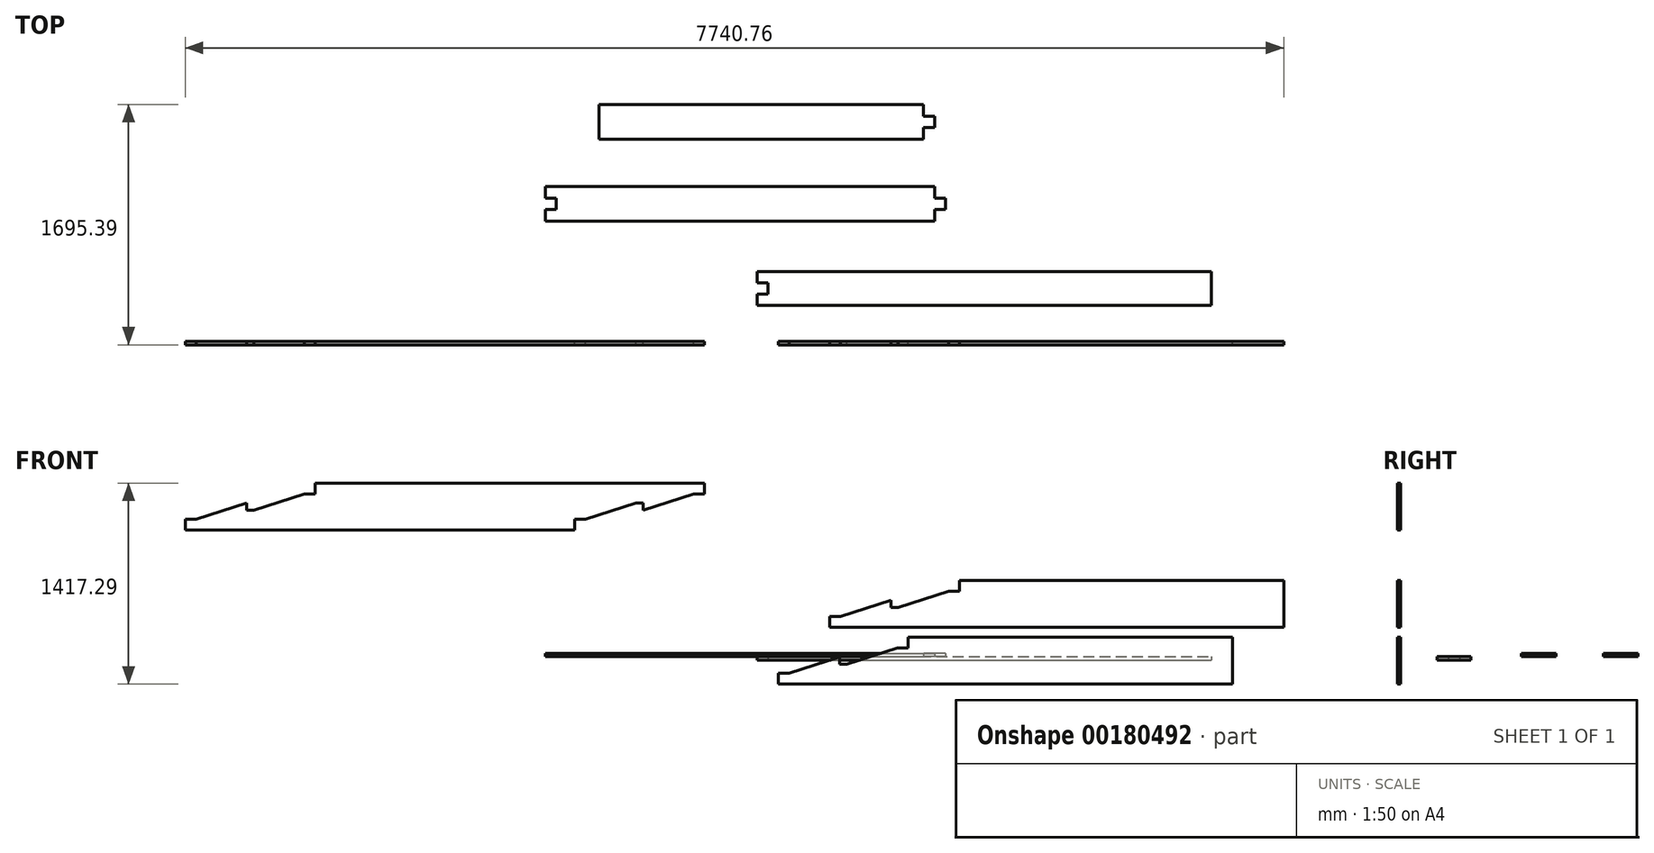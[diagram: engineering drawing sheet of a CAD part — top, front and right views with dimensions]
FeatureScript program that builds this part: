
annotation { "Feature Type Name" : "Feature", "Feature Type Description" : "" }
export const myFeature = defineFeature(function(context is Context, id is Id, definition is map)
    precondition{}
    {
        {
            var Q0;
            Q0=qCreatedBy(makeId("Front.planeOp"),FACE);
            var sketch = newSketch(context, id + "F0", { "sketchPlane" : qUnion([Q0])});
            skLineSegment(sketch, "E0.bottom", {"start": v(-614.36, 159.8) * mm, "end": v(1671.64, 159.8) * mm});
            skLineSegment(sketch, "E0.top", {"start": v(-1528.76, -170.4) * mm, "end": v(1671.64, -170.4) * mm});
            skLineSegment(sketch, "E0.left", {"start": v(-1528.76, -94.2) * mm, "end": v(-1528.76, -170.4) * mm});
            skLineSegment(sketch, "E0.right", {"start": v(1671.64, 159.8) * mm, "end": v(1671.64, -170.4) * mm});
            skLineSegment(sketch, "E1", {"start": v(-1528.76, -94.2) * mm, "end": v(-1452.56, -94.2) * mm});
            skLineSegment(sketch, "E2", {"start": v(-1452.56, -94.2) * mm, "end": v(-1096.96, 20.1) * mm});
            skLineSegment(sketch, "E3", {"start": v(-1096.96, 20.1) * mm, "end": v(-1096.96, -30.7) * mm});
            skLineSegment(sketch, "E4", {"start": v(-1096.96, -30.7) * mm, "end": v(-1046.16, -30.7) * mm});
            skLineSegment(sketch, "E5", {"start": v(-1046.16, -30.7) * mm, "end": v(-690.56, 83.6) * mm});
            skLineSegment(sketch, "E6", {"start": v(-690.56, 83.6) * mm, "end": v(-614.36, 83.6) * mm});
            skLineSegment(sketch, "E7", {"start": v(-614.36, 83.6) * mm, "end": v(-614.36, 159.8) * mm});
            skPoint(sketch, "E8.orphan", {"position": v(-1528.76, 159.8) * mm});
            skLineSegment(sketch, "E9.bottom", {"start": v(-254.29, 561.34) * mm, "end": v(2031.71, 561.34) * mm});
            skLineSegment(sketch, "E9.top", {"start": v(-1168.69, 231.14) * mm, "end": v(2031.71, 231.14) * mm});
            skLineSegment(sketch, "E9.left", {"start": v(-1168.69, 307.34) * mm, "end": v(-1168.69, 231.14) * mm});
            skLineSegment(sketch, "E9.right", {"start": v(2031.71, 561.34) * mm, "end": v(2031.71, 231.14) * mm});
            skLineSegment(sketch, "E10", {"start": v(-1168.69, 307.34) * mm, "end": v(-1092.49, 307.34) * mm});
            skLineSegment(sketch, "E11", {"start": v(-1092.49, 307.34) * mm, "end": v(-736.89, 421.64) * mm});
            skLineSegment(sketch, "E12", {"start": v(-736.89, 421.64) * mm, "end": v(-736.89, 370.84) * mm});
            skLineSegment(sketch, "E13", {"start": v(-736.89, 370.84) * mm, "end": v(-686.09, 370.84) * mm});
            skLineSegment(sketch, "E14", {"start": v(-686.09, 370.84) * mm, "end": v(-330.49, 485.14) * mm});
            skLineSegment(sketch, "E15", {"start": v(-330.49, 485.14) * mm, "end": v(-254.29, 485.14) * mm});
            skLineSegment(sketch, "E16", {"start": v(-254.29, 485.14) * mm, "end": v(-254.29, 561.34) * mm});
            skPoint(sketch, "E17.orphan", {"position": v(-1168.69, 561.34) * mm});
            skSolve(sketch);
        }
        {
            var Q0;
            Q0=makeQuery(id+"F0.imprint","IMPRINT",FACE,{"disambiguationData":[TD([[makeQuery(id+"F0.imprint","IMPRINT",EDGE,{"derivedFrom":sQuery(id+"F0.wireOp",EDGE,"E0.bottom")}),-1.0]])]});
            var Q1;
            Q1=makeQuery(id+"F0.imprint","IMPRINT",FACE,{"disambiguationData":[TD([[makeQuery(id+"F0.imprint","IMPRINT",EDGE,{"derivedFrom":sQuery(id+"F0.wireOp",EDGE,"E9.bottom")}),-1.0]])]});
            extrude(context, id + "F1", {"entities" : qUnion([Q0, Q1]), "depth" : 23.8 * mm});
        }
        {
            var Q0;
            Q0=makeQuery(id+"F0.imprint","IMPRINT",FACE,{"disambiguationData":[TD([[makeQuery(id+"F0.imprint","IMPRINT",EDGE,{"derivedFrom":sQuery(id+"F0.wireOp",EDGE,"E0.bottom")}),-1.0]])]});
            var sketch = newSketch(context, id + "F2", { "sketchPlane" : qUnion([Q0])});
            skLineSegment(sketch, "E18.bottom", {"start": v(-4794.65, 1246.88) * mm, "end": v(-2051.45, 1246.88) * mm});
            skLineSegment(sketch, "E18.top", {"start": v(-5709.05, 916.68) * mm, "end": v(-2965.85, 916.68) * mm});
            skLineSegment(sketch, "E18.left", {"start": v(-5709.05, 992.88) * mm, "end": v(-5709.05, 916.68) * mm});
            skLineSegment(sketch, "E18.right", {"start": v(-2051.45, 1246.88) * mm, "end": v(-2051.45, 1170.68) * mm});
            skLineSegment(sketch, "E19", {"start": v(-2965.85, 916.68) * mm, "end": v(-2965.85, 992.88) * mm});
            skLineSegment(sketch, "E20", {"start": v(-2965.85, 992.88) * mm, "end": v(-2889.65, 992.88) * mm});
            skLineSegment(sketch, "E21", {"start": v(-2889.65, 992.88) * mm, "end": v(-2534.05, 1107.18) * mm});
            skLineSegment(sketch, "E22", {"start": v(-2483.25, 1056.38) * mm, "end": v(-2127.65, 1170.68) * mm});
            skLineSegment(sketch, "E23", {"start": v(-2127.65, 1170.68) * mm, "end": v(-2051.45, 1170.68) * mm});
            skLineSegment(sketch, "E24", {"start": v(-5709.05, 992.88) * mm, "end": v(-5632.85, 992.88) * mm});
            skLineSegment(sketch, "E25", {"start": v(-5632.85, 992.88) * mm, "end": v(-5277.25, 1107.18) * mm});
            skLineSegment(sketch, "E26", {"start": v(-5277.25, 1107.18) * mm, "end": v(-5277.25, 1056.38) * mm});
            skLineSegment(sketch, "E27", {"start": v(-5277.25, 1056.38) * mm, "end": v(-5226.45, 1056.38) * mm});
            skLineSegment(sketch, "E28", {"start": v(-5226.45, 1056.38) * mm, "end": v(-4870.85, 1170.68) * mm});
            skLineSegment(sketch, "E29", {"start": v(-4870.85, 1170.68) * mm, "end": v(-4794.65, 1170.68) * mm});
            skLineSegment(sketch, "E30", {"start": v(-4794.65, 1170.68) * mm, "end": v(-4794.65, 1246.88) * mm});
            skLineSegment(sketch, "E31.0", {"start": v(-2483.25, 1107.18) * mm, "end": v(-2483.25, 1056.38) * mm});
            skLineSegment(sketch, "E32.0", {"start": v(-2534.05, 1107.18) * mm, "end": v(-2483.25, 1107.18) * mm});
            skSolve(sketch);
        }
        {
            var Q0;
            Q0=makeQuery(id+"F2.imprint","IMPRINT",FACE,{"disambiguationData":[TD([[makeQuery(id+"F2.imprint","IMPRINT",EDGE,{"derivedFrom":sQuery(id+"F2.wireOp",EDGE,"E18.bottom")}),-1.0]])]});
            extrude(context, id + "F3", {"entities" : qUnion([Q0]), "depth" : 23.8 * mm});
        }
        {
            var Q0;
            Q0=qCreatedBy(makeId("Top.planeOp"),FACE);
            var sketch = newSketch(context, id + "F4", { "sketchPlane" : qUnion([Q0])});
            skLineSegment(sketch, "E33.bottom", {"start": v(-1680.17, 493.1) * mm, "end": v(1520.23, 493.1) * mm});
            skLineSegment(sketch, "E33.top", {"start": v(-1680.17, 254.98) * mm, "end": v(1520.23, 254.98) * mm});
            skLineSegment(sketch, "E33.left", {"start": v(-1680.17, 493.1) * mm, "end": v(-1680.17, 413.73) * mm});
            skLineSegment(sketch, "E33.right", {"start": v(1520.23, 493.1) * mm, "end": v(1520.23, 254.98) * mm});
            skLineSegment(sketch, "E34", {"start": v(-1680.17, 413.73) * mm, "end": v(-1603.97, 413.73) * mm});
            skPoint(sketch, "E34.endSnap0", {"position": v(-1603.97, 374.04) * mm});
            skLineSegment(sketch, "E35", {"start": v(-1603.97, 413.73) * mm, "end": v(-1603.97, 334.35) * mm});
            skLineSegment(sketch, "E36", {"start": v(-1603.97, 334.35) * mm, "end": v(-1680.17, 334.35) * mm});
            skLineSegment(sketch, "E37.trimOffspring", {"start": v(-1680.17, 334.35) * mm, "end": v(-1680.17, 254.98) * mm});
            skSolve(sketch);
        }
        {
            var Q0;
            Q0 = qSketchRegion(id + "F4", true);
            extrude(context, id + "F5", {"entities" : qUnion([Q0]), "depth" : 23.8 * mm});
        }
        {
            var Q0;
            Q0=makeQuery(id+"F5.opExtrude","CAP_FACE",FACE,{"disambiguationData":[OSD([sQuery(id+"F4.wireOp",EDGE,"E33.bottom"),sQuery(id+"F4.wireOp",EDGE,"E33.top"),sQuery(id+"F4.wireOp",EDGE,"E33.left"),sQuery(id+"F4.wireOp",EDGE,"E33.right"),sQuery(id+"F4.wireOp",EDGE,"E34"),sQuery(id+"F4.wireOp",EDGE,"E35"),sQuery(id+"F4.wireOp",EDGE,"E36"),sQuery(id+"F4.wireOp",EDGE,"E37.trimOffspring")])],"isStart":false});
            var sketch = newSketch(context, id + "F6", { "sketchPlane" : qUnion([Q0])});
            skLineSegment(sketch, "E38.bottom", {"start": v(-3172.31, 1093.73) * mm, "end": v(-429.11, 1093.73) * mm});
            skLineSegment(sketch, "E38.top", {"start": v(-3172.31, 848.8) * mm, "end": v(-429.11, 848.8) * mm});
            skLineSegment(sketch, "E38.left", {"start": v(-3172.31, 1093.73) * mm, "end": v(-3172.31, 1012.08) * mm});
            skLineSegment(sketch, "E38.right", {"start": v(-350.74, 1012.08) * mm, "end": v(-350.74, 930.44) * mm});
            skLineSegment(sketch, "E39", {"start": v(-3172.31, 1012.08) * mm, "end": v(-3093.94, 1012.08) * mm});
            skPoint(sketch, "E39.endSnap0", {"position": v(-3093.94, 971.26) * mm});
            skLineSegment(sketch, "E40", {"start": v(-3093.94, 1012.08) * mm, "end": v(-3093.94, 930.44) * mm});
            skLineSegment(sketch, "E41", {"start": v(-3093.94, 930.44) * mm, "end": v(-3172.31, 930.44) * mm});
            skLineSegment(sketch, "E42", {"start": v(-350.74, 1012.08) * mm, "end": v(-429.11, 1012.08) * mm});
            skLineSegment(sketch, "E43", {"start": v(-429.11, 1012.08) * mm, "end": v(-429.11, 1093.73) * mm});
            skLineSegment(sketch, "E44", {"start": v(-350.74, 930.44) * mm, "end": v(-429.11, 930.44) * mm});
            skLineSegment(sketch, "E45", {"start": v(-429.11, 930.44) * mm, "end": v(-429.11, 848.8) * mm});
            skLineSegment(sketch, "E46.trimOffspring", {"start": v(-3172.31, 930.44) * mm, "end": v(-3172.31, 848.8) * mm});
            skLineSegment(sketch, "E47.bottom", {"start": v(-2793.1, 1671.58) * mm, "end": v(-507.1, 1671.58) * mm});
            skLineSegment(sketch, "E47.top", {"start": v(-2793.1, 1426.65) * mm, "end": v(-507.1, 1426.65) * mm});
            skLineSegment(sketch, "E47.right", {"start": v(-428.72, 1589.93) * mm, "end": v(-428.72, 1508.3) * mm});
            skPoint(sketch, "E48.endSnap0", {"position": v(-3171.92, -23.54) * mm});
            skLineSegment(sketch, "E49", {"start": v(-428.72, 1589.93) * mm, "end": v(-507.1, 1589.93) * mm});
            skLineSegment(sketch, "E50", {"start": v(-507.1, 1589.93) * mm, "end": v(-507.1, 1671.58) * mm});
            skLineSegment(sketch, "E51", {"start": v(-428.72, 1508.3) * mm, "end": v(-507.1, 1508.3) * mm});
            skLineSegment(sketch, "E52", {"start": v(-507.1, 1508.3) * mm, "end": v(-507.1, 1426.65) * mm});
            skLineSegment(sketch, "E53", {"start": v(-2793.1, 1426.65) * mm, "end": v(-2793.1, 1671.58) * mm});
            skPoint(sketch, "E48.end.orphan", {"position": v(-3171.92, 1589.93) * mm});
            skSolve(sketch);
        }
        {
            var Q0;
            Q0 = qSketchRegion(id + "F6", true);
            extrude(context, id + "F7", {"entities" : qUnion([Q0]), "depth" : 23.8 * mm});
        }
    });
